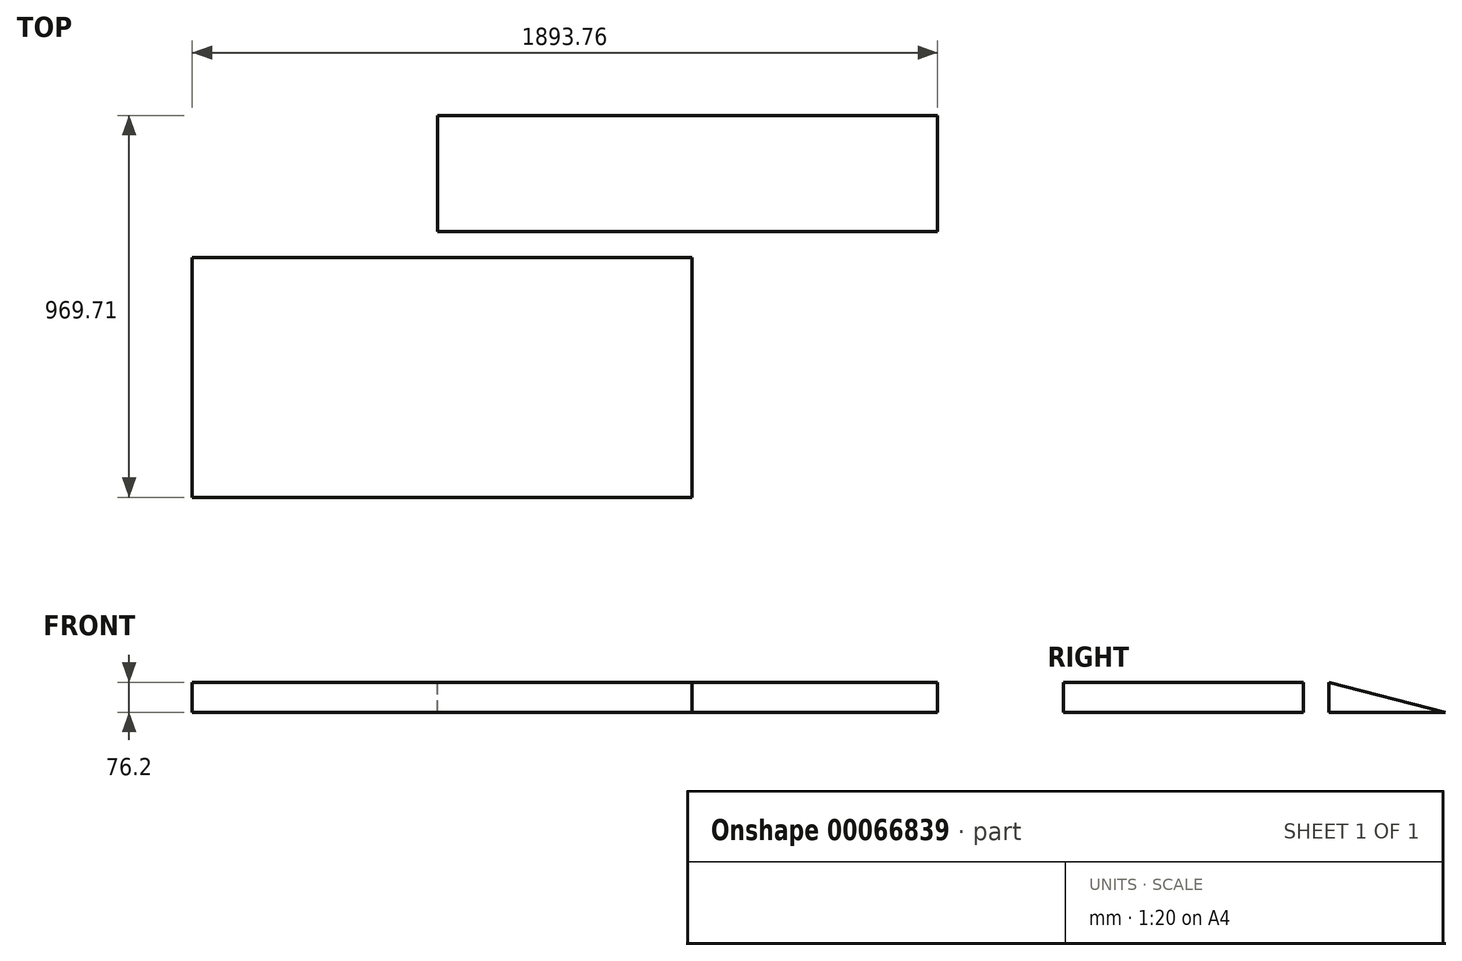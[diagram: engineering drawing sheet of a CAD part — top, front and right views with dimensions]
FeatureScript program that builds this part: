
annotation { "Feature Type Name" : "Feature", "Feature Type Description" : "" }
export const myFeature = defineFeature(function(context is Context, id is Id, definition is map)
    precondition{}
    {
        {
            var Q0;
            Q0=qCreatedBy(makeId("Top.planeOp"),FACE);
            var sketch = newSketch(context, id + "F0", { "sketchPlane" : qUnion([Q0])});
            skLineSegment(sketch, "E0.bottom", {"start": v(-623.76, -303.23) * mm, "end": v(646.24, -303.23) * mm});
            skLineSegment(sketch, "E0.top", {"start": v(-623.76, 306.37) * mm, "end": v(646.24, 306.37) * mm});
            skLineSegment(sketch, "E0.left", {"start": v(-623.76, -303.23) * mm, "end": v(-623.76, 306.37) * mm});
            skLineSegment(sketch, "E0.right", {"start": v(646.24, -303.23) * mm, "end": v(646.24, 306.37) * mm});
            skSolve(sketch);
        }
        {
            var Q0;
            Q0=makeQuery(id+"F0.imprint","IMPRINT",FACE,{"disambiguationData":[TD([[makeQuery(id+"F0.imprint","IMPRINT",EDGE,{"derivedFrom":sQuery(id+"F0.wireOp",EDGE,"E0.bottom")}),1.0]])]});
            extrude(context, id + "F1", {"entities" : qUnion([Q0]), "depth" : 76.2 * mm});
        }
        {
            var Q0;
            Q0=qCreatedBy(makeId("Right.planeOp"),FACE);
            var sketch = newSketch(context, id + "F2", { "sketchPlane" : qUnion([Q0])});
            skLineSegment(sketch, "E1", {"start": v(371.36, 0) * mm, "end": v(371.36, 76.2) * mm});
            skLineSegment(sketch, "E2", {"start": v(371.36, 76.2) * mm, "end": v(666.48, 0) * mm});
            skLineSegment(sketch, "E3", {"start": v(666.48, 0) * mm, "end": v(371.36, 0) * mm});
            skSolve(sketch);
        }
        {
            var Q0;
            Q0=makeQuery(id+"F2.imprint","IMPRINT",FACE,{"disambiguationData":[TD([[makeQuery(id+"F2.imprint","IMPRINT",EDGE,{"derivedFrom":sQuery(id+"F2.wireOp",EDGE,"E1")}),-1.0]])]});
            extrude(context, id + "F3", {"entities" : qUnion([Q0]), "depth" : 1270 * mm});
        }
    });
